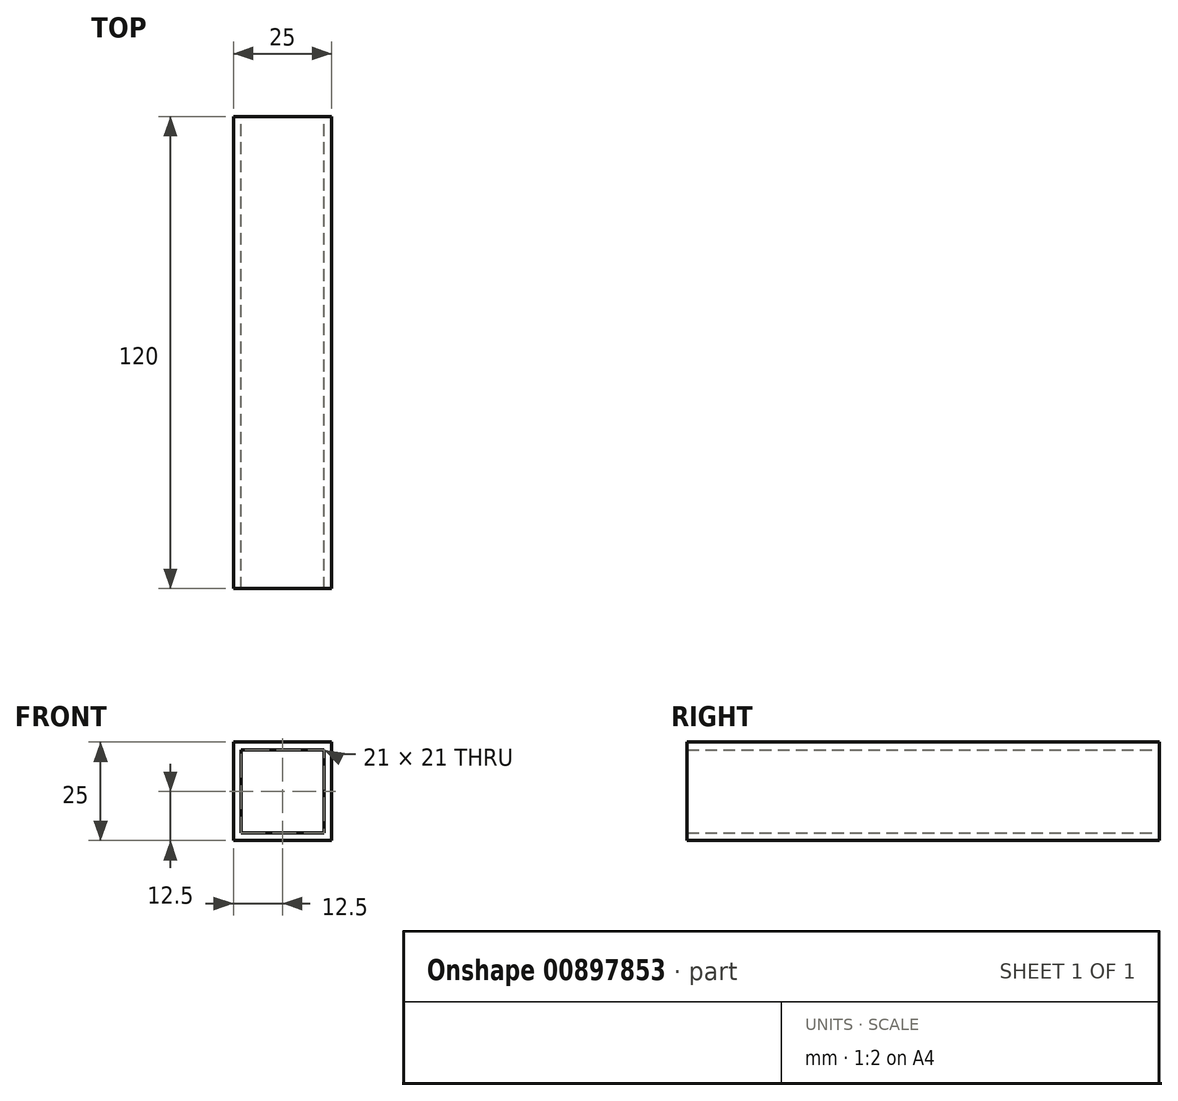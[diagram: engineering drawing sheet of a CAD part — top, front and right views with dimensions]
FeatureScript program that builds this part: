
annotation { "Feature Type Name" : "Feature", "Feature Type Description" : "" }
export const myFeature = defineFeature(function(context is Context, id is Id, definition is map)
    precondition{}
    {
        {
            var Q0;
            Q0=qCreatedBy(makeId("Front.planeOp"),FACE);
            var sketch = newSketch(context, id + "F0", { "sketchPlane" : qUnion([Q0])});
            skLineSegment(sketch, "E0.bottom", {"start": v(12.5, -12.5) * mm, "end": v(-12.5, -12.5) * mm});
            skLineSegment(sketch, "E0.top", {"start": v(12.5, 12.5) * mm, "end": v(-12.5, 12.5) * mm});
            skLineSegment(sketch, "E0.left", {"start": v(12.5, -12.5) * mm, "end": v(12.5, 12.5) * mm});
            skLineSegment(sketch, "E0.right", {"start": v(-12.5, -12.5) * mm, "end": v(-12.5, 12.5) * mm});
            skPoint(sketch, "E0.middle", {"position": v(0, 0) * mm});
            skLineSegment(sketch, "E1.0", {"start": v(10.5, 10.5) * mm, "end": v(-10.5, 10.5) * mm});
            skLineSegment(sketch, "E1.1", {"start": v(10.5, -10.5) * mm, "end": v(10.5, 10.5) * mm});
            skLineSegment(sketch, "E1.2", {"start": v(10.5, -10.5) * mm, "end": v(-10.5, -10.5) * mm});
            skLineSegment(sketch, "E1.3", {"start": v(-10.5, -10.5) * mm, "end": v(-10.5, 10.5) * mm});
            skSolve(sketch);
        }
        {
            var Q0;
            Q0=qSketchRegion(id+"F0",true);
            extrude(context, id + "F1", {"entities" : qUnion([Q0]), "depth" : 60 * mm, "offsetDistance" : 25 * mm, "hasSecondDirection" : true, "secondDirectionOppositeDirection" : true, "secondDirectionDepth" : 60 * mm});
        }
    });
